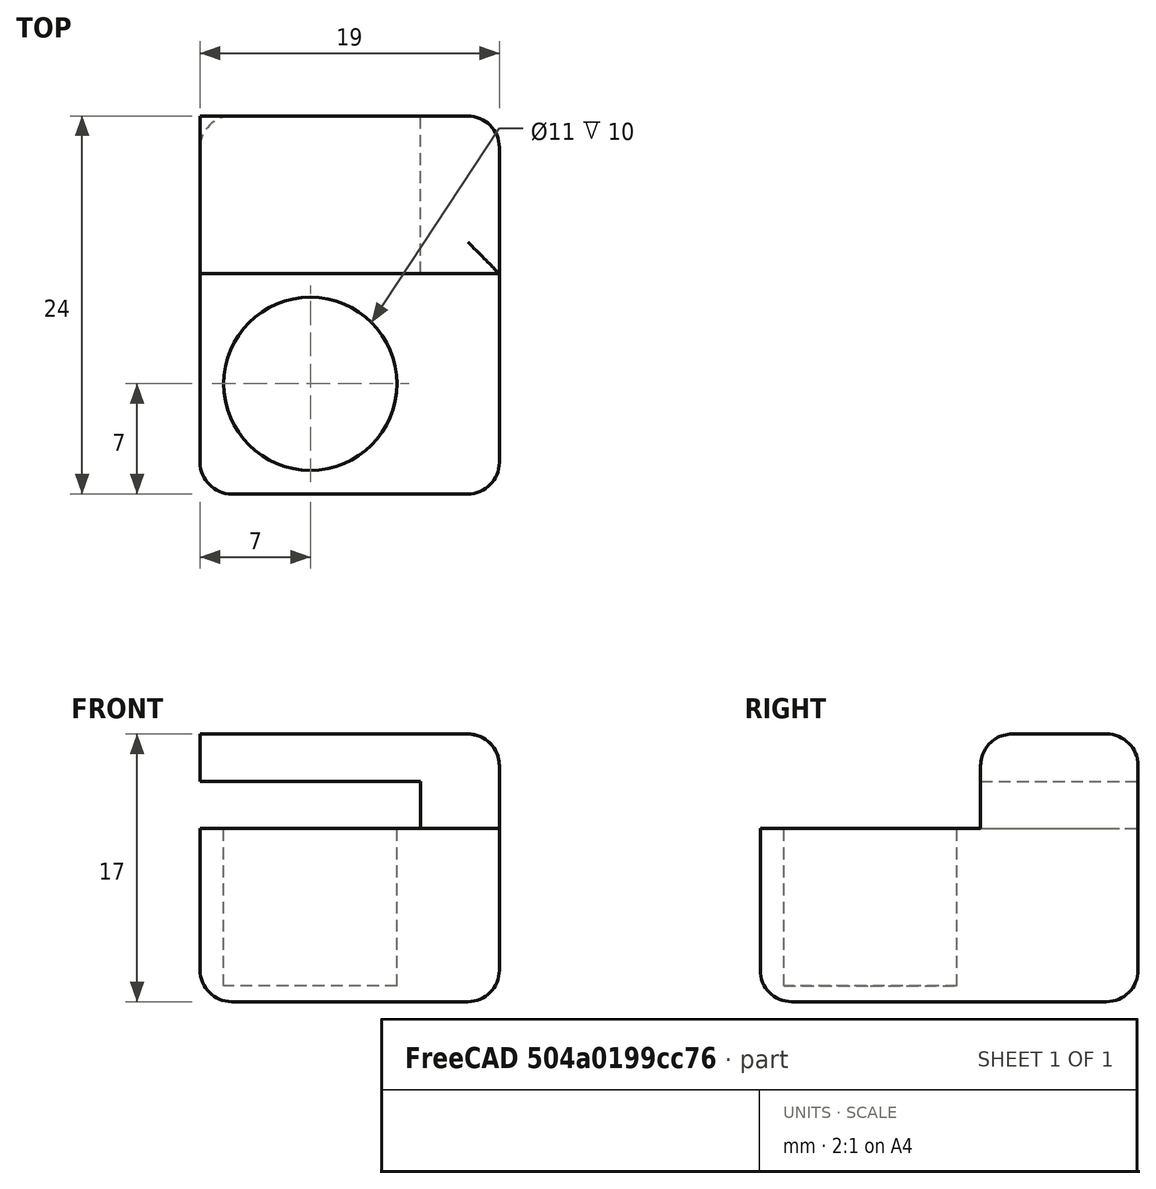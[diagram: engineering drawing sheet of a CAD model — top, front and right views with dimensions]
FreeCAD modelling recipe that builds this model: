
FCSTD DOCUMENT  (FreeCAD 0.19R)
Label: StripAnchor
License: All rights reserved
LicenseURL: http://en.wikipedia.org/wiki/All_rights_reserved
objects: Part::Box×3, Part::Cylinder×1, Part::MultiFuse×1, Part::Cut×1, Part::Fillet×1
note: 7 computed .brp shape members not serialized (recipe doc carries the construction recipe); baked Part::Feature solids carry a one-line shape summary decoded from their .brp

FEATURE [Part::Box] Box  label="Main Base Raw"
  AttacherType = Attacher::AttachEngine3D
  Height = 11
  Length = 19
  Width = 24
FEATURE [Part::Cylinder] Cylinder  label="Magnet Hole"
  Angle = 360
  AttacherType = Attacher::AttachEngine3D
  Height = 10
  Placement = pos=(7,7,1) rot=(0,0,1;0rad)
  Radius = 5.5
FEATURE [Part::Box] Box001  label="Cube001"
  AttacherType = Attacher::AttachEngine3D
  Height = 3
  Length = 5
  Placement = pos=(14,14,11) rot=(0,0,1;0rad)
  Width = 10
FEATURE [Part::Box] Box002  label="Cube002"
  AttacherType = Attacher::AttachEngine3D
  Height = 3
  Length = 19
  Placement = pos=(0,14,14) rot=(0,0,1;0rad)
  Width = 10
FEATURE [Part::MultiFuse] Fusion
  Shapes = -> [Box,Box001,Box002]
FEATURE [Part::Cut] Cut
  Base = -> Fusion
  Tool = -> Cylinder
FEATURE [Part::Fillet] Fillet
  Base = -> Cut
  Edges = 13 edges r=2: [Edge1,Edge3,Edge4,Edge5,Edge6,Edge13,Edge14,Edge16,Edge25,Edge32,Edge34,Edge35,Edge37]
